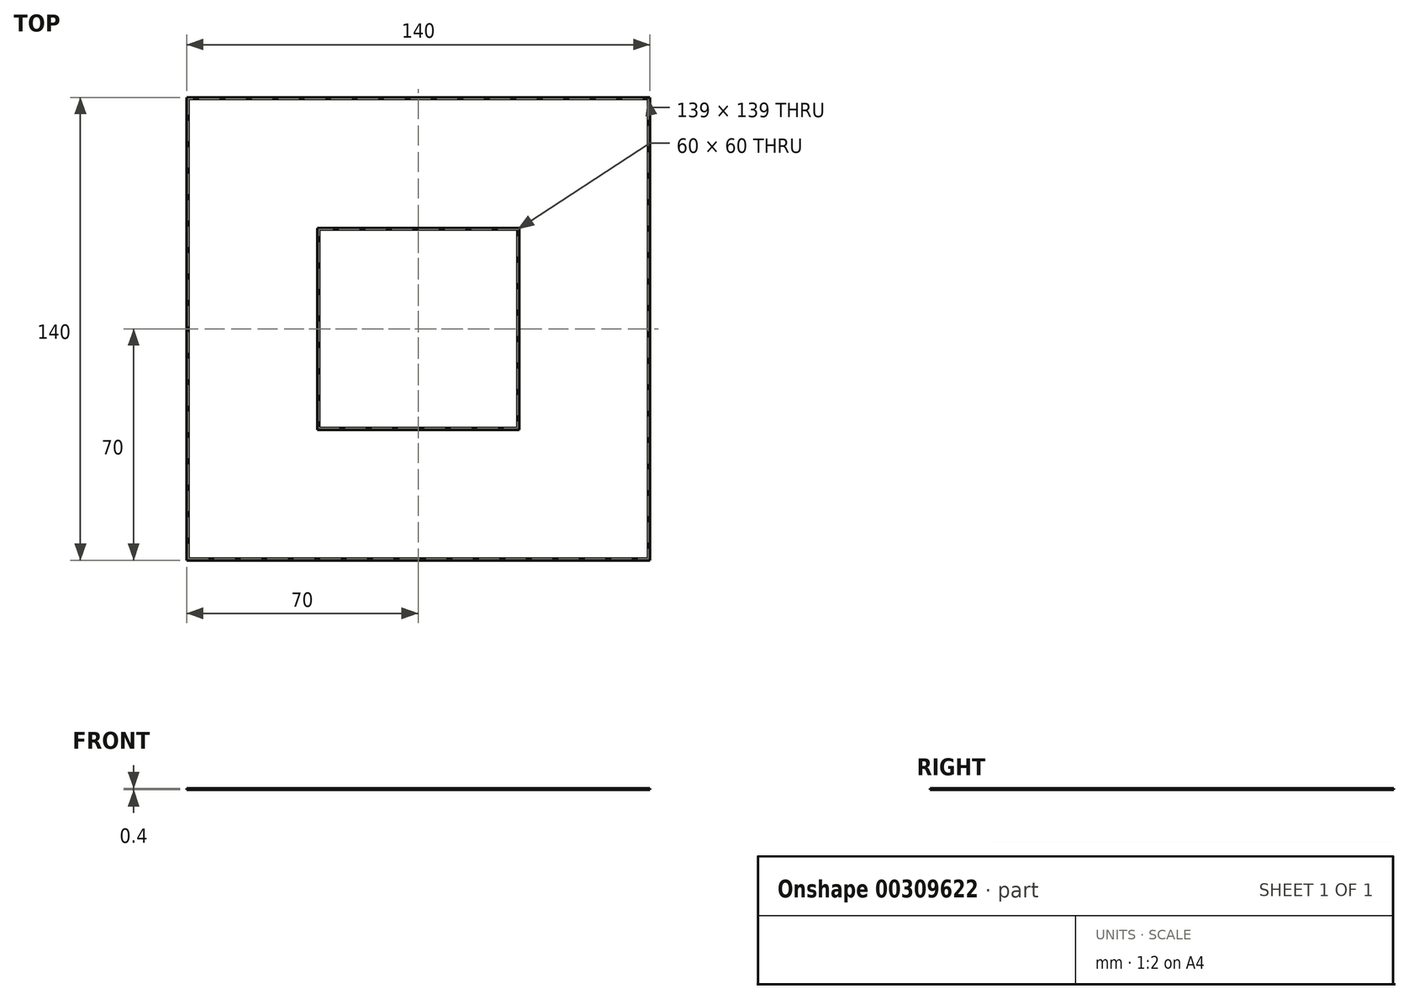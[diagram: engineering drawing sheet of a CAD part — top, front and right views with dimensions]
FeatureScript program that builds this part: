
annotation { "Feature Type Name" : "Feature", "Feature Type Description" : "" }
export const myFeature = defineFeature(function(context is Context, id is Id, definition is map)
    precondition{}
    {
        {
            var Q0;
            Q0=qCreatedBy(makeId("Top.planeOp"),FACE);
            var sketch = newSketch(context, id + "F0", { "sketchPlane" : qUnion([Q0])});
            skLineSegment(sketch, "E0.bottom", {"start": v(70, -70) * mm, "end": v(-70, -70) * mm});
            skLineSegment(sketch, "E0.top", {"start": v(70, 70) * mm, "end": v(-70, 70) * mm});
            skLineSegment(sketch, "E0.left", {"start": v(70, -70) * mm, "end": v(70, 70) * mm});
            skLineSegment(sketch, "E0.right", {"start": v(-70, -70) * mm, "end": v(-70, 70) * mm});
            skPoint(sketch, "E0.middle", {"position": v(0, 0) * mm});
            skLineSegment(sketch, "E1.bottom", {"start": v(69.5, -69.5) * mm, "end": v(-69.5, -69.5) * mm});
            skLineSegment(sketch, "E1.top", {"start": v(69.5, 69.5) * mm, "end": v(-69.5, 69.5) * mm});
            skLineSegment(sketch, "E1.left", {"start": v(69.5, -69.5) * mm, "end": v(69.5, 69.5) * mm});
            skLineSegment(sketch, "E1.right", {"start": v(-69.5, -69.5) * mm, "end": v(-69.5, 69.5) * mm});
            skLineSegment(sketch, "E2.bottom", {"start": v(30.5, -30.5) * mm, "end": v(-30.5, -30.5) * mm});
            skLineSegment(sketch, "E2.top", {"start": v(30.5, 30.5) * mm, "end": v(-30.5, 30.5) * mm});
            skLineSegment(sketch, "E2.left", {"start": v(30.5, -30.5) * mm, "end": v(30.5, 30.5) * mm});
            skLineSegment(sketch, "E2.right", {"start": v(-30.5, -30.5) * mm, "end": v(-30.5, 30.5) * mm});
            skLineSegment(sketch, "E3.bottom", {"start": v(30, -30) * mm, "end": v(-30, -30) * mm});
            skLineSegment(sketch, "E3.top", {"start": v(30, 30) * mm, "end": v(-30, 30) * mm});
            skLineSegment(sketch, "E3.left", {"start": v(30, -30) * mm, "end": v(30, 30) * mm});
            skLineSegment(sketch, "E3.right", {"start": v(-30, -30) * mm, "end": v(-30, 30) * mm});
            skSolve(sketch);
        }
        {
            var Q0;
            Q0=makeQuery(id+"F0.imprint","IMPRINT",FACE,{"disambiguationData":[TD([[makeQuery(id+"F0.imprint","IMPRINT",EDGE,{"derivedFrom":sQuery(id+"F0.wireOp",EDGE,"E0.bottom")}),-1.0]])]});
            var Q1;
            Q1=makeQuery(id+"F0.imprint","IMPRINT",FACE,{"disambiguationData":[TD([[makeQuery(id+"F0.imprint","IMPRINT",EDGE,{"derivedFrom":sQuery(id+"F0.wireOp",EDGE,"E2.bottom")}),-1.0]])]});
            extrude(context, id + "F1", {"entities" : qUnion([Q0, Q1]), "depth" : 0.4 * mm});
        }
    });
